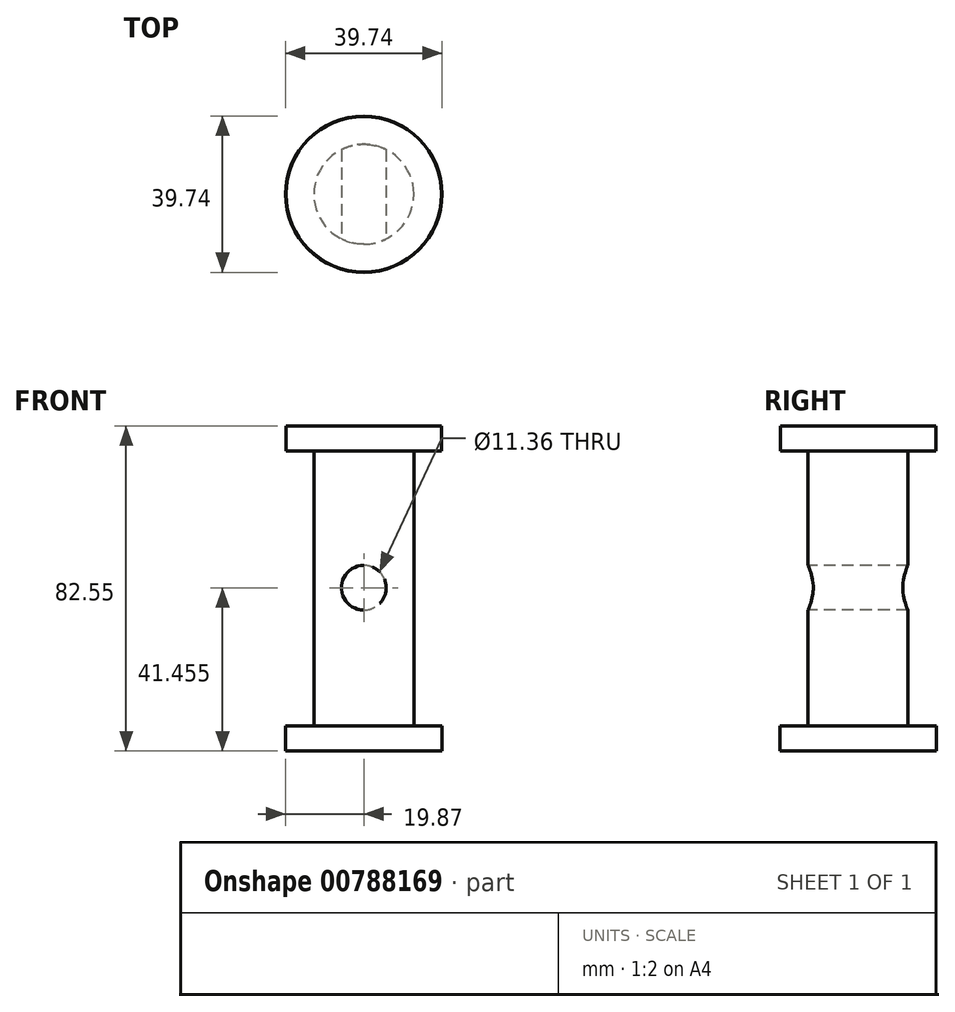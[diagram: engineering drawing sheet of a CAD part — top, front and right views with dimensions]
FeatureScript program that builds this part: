
annotation { "Feature Type Name" : "Feature", "Feature Type Description" : "" }
export const myFeature = defineFeature(function(context is Context, id is Id, definition is map)
    precondition{}
    {
        {
            var Q0;
            Q0=qCreatedBy(makeId("Top.planeOp"),FACE);
            var sketch = newSketch(context, id + "F0", { "sketchPlane" : qUnion([Q0])});
            skCircle(sketch, "E0", {"center": v(0, 0) * mm, "radius": 12.7 * mm});
            skSolve(sketch);
        }
        {
            var Q0;
            Q0=makeQuery(id+"F0.imprint","IMPRINT",FACE,{"disambiguationData":[TD([[makeQuery(id+"F0.imprint","IMPRINT",EDGE,{"derivedFrom":sQuery(id+"F0.wireOp",EDGE,"E0")}),1.0]])]});
            extrude(context, id + "F1", {"entities" : qUnion([Q0]), "depth" : 76.2 * mm, "offsetDistance" : 25.4 * mm});
        }
        {
            var Q0;
            Q0=qCreatedBy(makeId("Top.planeOp"),FACE);
            var sketch = newSketch(context, id + "F2", { "sketchPlane" : qUnion([Q0])});
            skCircle(sketch, "E1", {"center": v(0, 0) * mm, "radius": 19.87 * mm});
            skSolve(sketch);
        }
        {
            var Q0;
            Q0 = qSketchRegion(id + "F2", true);
            extrude(context, id + "F3", {"entities" : qUnion([Q0]), "operationType" : NewBodyOperationType.ADD, "depth" : 6.35 * mm, "offsetDistance" : 25.4 * mm});
        }
        {
            var Q0;
            Q0=makeQuery(id+"F1.opExtrude","CAP_FACE",FACE,{"disambiguationData":[OSD([sQuery(id+"F0.wireOp",EDGE,"E0")])],"isStart":false});
            var sketch = newSketch(context, id + "F4", { "sketchPlane" : qUnion([Q0])});
            skCircle(sketch, "E2", {"center": v(0, 0) * mm, "radius": 19.77 * mm});
            skSolve(sketch);
        }
        {
            var Q0;
            Q0 = qSketchRegion(id + "F4", true);
            extrude(context, id + "F5", {"entities" : qUnion([Q0]), "operationType" : NewBodyOperationType.ADD, "depth" : 6.35 * mm, "offsetDistance" : 25.4 * mm});
        }
        {
            var Q0;
            Q0=qCreatedBy(makeId("Front.planeOp"),FACE);
            var sketch = newSketch(context, id + "F6", { "sketchPlane" : qUnion([Q0])});
            skCircle(sketch, "E3", {"center": v(0, 41.45) * mm, "radius": 5.68 * mm});
            skSolve(sketch);
        }
        {
            var Q0;
            Q0 = qSketchRegion(id + "F6", true);
            extrude(context, id + "F7", {"entities" : qUnion([Q0]), "operationType" : NewBodyOperationType.REMOVE, "oppositeDirection" : true, "depth" : 508 * mm, "offsetDistance" : 25.4 * mm});
        }
        {
            var Q0;
            Q0=makeQuery(id+"F7.boolean.opBoolean","COPY",FACE,{"derivedFrom":makeQuery(id+"F7.opExtrude","CAP_FACE",FACE,{"disambiguationData":[OSD([sQuery(id+"F6.wireOp",EDGE,"E3")])],"isStart":true})});
            extrude(context, id + "F8", {"entities" : qUnion([Q0]), "operationType" : NewBodyOperationType.REMOVE, "oppositeDirection" : true, "depth" : 1270 * mm, "offsetDistance" : 25.4 * mm});
        }
    });
